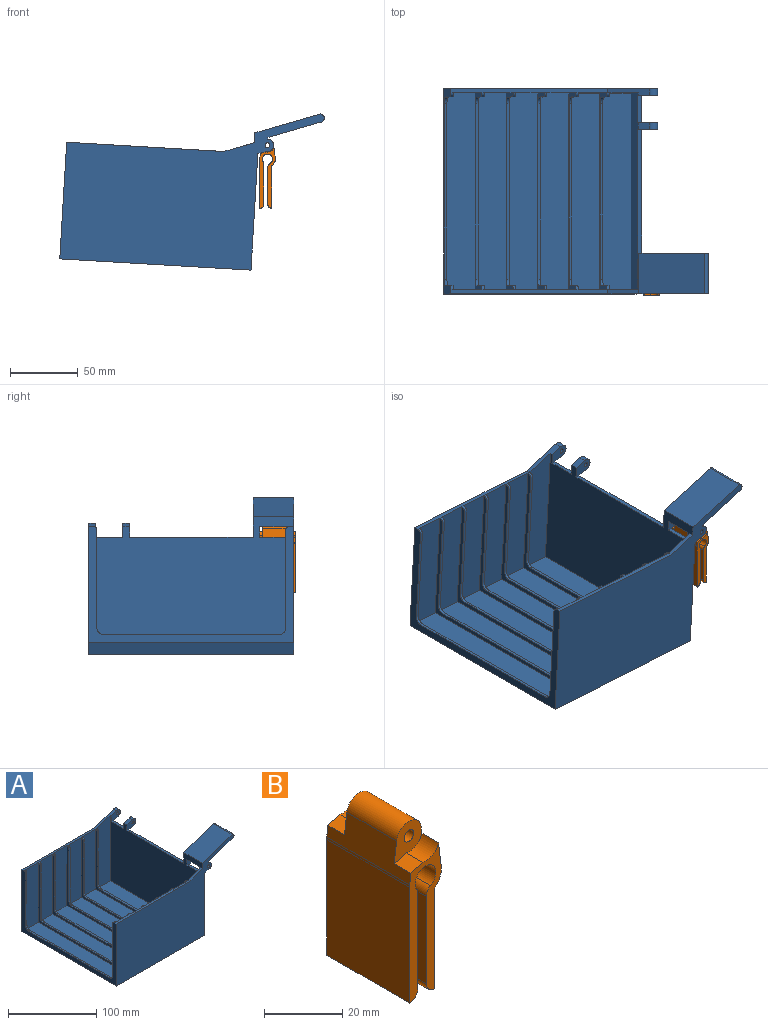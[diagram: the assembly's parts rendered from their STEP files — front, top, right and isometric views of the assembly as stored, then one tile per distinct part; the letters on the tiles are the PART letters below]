
ASSEMBLY  parts=2 mates=1
PART A: 109 faces, bbox 188.2x151x117.8 mm
  f0: cylinder r=4.5mm len=8.84mm, axis (0,1,0), area 64.7mm2, adj f89,f91,f92,f104
  f1: cylinder r=5mm len=20mm, axis (0,-1,0), area 79.2mm2, adj f88,f91,f104,f108
  f2: cylinder r=4.5mm len=8.84mm, axis (0,-1,0), area 64.7mm2, adj f8,f85,f88,f104
  f3: plane 91x3mm, normal (0,0,1), area 273mm2, adj f9,f26,f92,f103
  f4: plane 116x3mm, normal (0,0,1), area 348mm2, adj f10,f11,f14,f16,f19,f22,f29,f49
  f5: plane 20x3mm, normal (0,0,1), area 60mm2, adj f9,f26,f97,f102
  f6: plane 20x3mm, normal (0,0,1), area 60mm2, adj f9,f26,f88,f91
  f7: plane 145x83mm, normal (1,0,0), area 921.9mm2, adj f25,f27,f40,f43,f44,f45,f46,f47
  f8: plane 188.25x117.81mm, normal (0,-1,0), area 12641.2mm2, adj f2,f9,f11,f12,f26,f36,f85,f86
  f9: plane 151x86mm, normal (1,0,0), area 12986mm2, adj f3,f5,f6,f8,f10,f12,f85,f89
  f10: plane 152.25x97mm, normal (0,1,0), area 12320.9mm2, adj f4,f9,f11,f12,f93,f94,f95,f96
  f11: plane 151x86mm, normal (-1,0,0), area 1872.9mm2, adj f4,f8,f10,f12,f36,f71,f72,f73
  f12: plane 151x141mm, normal (0,0,-1), area 21291mm2, adj f8,f9,f10,f11
  f13: plane 145x83mm, normal (1,0,0), area 921.9mm2, adj f14,f35,f42,f78,f79,f80,f81,f82
  f14: plane 83x21mm, normal (0,-1,0), area 1743mm2, adj f4,f13,f15,f42
  f15: plane 145x83mm, normal (-1,0,0), area 921.9mm2, adj f14,f35,f42,f43,f44,f45,f46,f47
  f16: plane 83x21mm, normal (0,-1,0), area 1743mm2, adj f4,f17,f31,f37
  f17: plane 145x83mm, normal (-1,0,0), area 921.9mm2, adj f16,f18,f37,f78,f79,f80,f81,f82
  f18: plane 83x21mm, normal (0,1,0), area 1743mm2, adj f17,f31,f36,f37
  f19: plane 83x21mm, normal (0,-1,0), area 1743mm2, adj f4,f20,f32,f38
  f20: plane 145x83mm, normal (-1,0,0), area 921.9mm2, adj f19,f21,f38,f64,f65,f66,f67,f68
  f21: plane 83x21mm, normal (0,1,0), area 1743mm2, adj f20,f32,f36,f38
  f22: plane 83x21mm, normal (0,-1,0), area 1743mm2, adj f4,f23,f33,f39
  f23: plane 145x83mm, normal (-1,0,0), area 921.9mm2, adj f22,f24,f39,f57,f58,f59,f60,f61
  f24: plane 83x21mm, normal (0,1,0), area 1743mm2, adj f23,f33,f36,f39
  f25: plane 90.81x22mm, normal (0,-1,0), area 1828.9mm2, adj f7,f26,f40,f49,f96
  f26: plane 148x98.07mm, normal (-1,0,0), area 12362.2mm2, adj f3,f5,f6,f8,f25,f27,f40,f87
  f27: plane 90.81x22mm, normal (0,1,0), area 1828.9mm2, adj f7,f26,f40,f48,f87
  f28: plane 145x83mm, normal (1,0,0), area 921.9mm2, adj f29,f34,f41,f71,f72,f73,f74,f75
  f29: plane 83x21mm, normal (0,-1,0), area 1743mm2, adj f4,f28,f30,f41
  f30: plane 145x83mm, normal (-1,0,0), area 921.9mm2, adj f29,f34,f41,f50,f51,f52,f53,f54
  f31: plane 145x83mm, normal (1,0,0), area 921.9mm2, adj f16,f18,f37,f64,f65,f66,f67,f68
  f32: plane 145x83mm, normal (1,0,0), area 921.9mm2, adj f19,f21,f38,f57,f58,f59,f60,f61
  f33: plane 145x83mm, normal (1,0,0), area 921.9mm2, adj f22,f24,f39,f50,f51,f52,f53,f54
  f34: plane 83x21mm, normal (0,1,0), area 1743mm2, adj f28,f30,f36,f41
  f35: plane 83x21mm, normal (0,1,0), area 1743mm2, adj f13,f15,f36,f42
  f36: plane 116x3mm, normal (0,0,1), area 348mm2, adj f8,f11,f18,f21,f24,f34,f35,f48
  f37: plane 145x21mm, normal (0,0,1), area 3045mm2, adj f16,f17,f18,f31
  f38: plane 145x21mm, normal (0,0,1), area 3045mm2, adj f19,f20,f21,f32
  f39: plane 145x21mm, normal (0,0,1), area 3045mm2, adj f22,f23,f24,f33
  f40: plane 145x21mm, normal (0,0,1), area 3045mm2, adj f7,f25,f26,f27
  f41: plane 145x21mm, normal (0,0,1), area 3045mm2, adj f28,f29,f30,f34
  f42: plane 145x21mm, normal (0,0,1), area 3045mm2, adj f13,f14,f15,f35
  f43: plane 72x2mm, normal (0,1,0), area 144mm2, adj f7,f15,f44,f48
  f44: cylinder r=5mm len=5mm, axis (-1,0,0), area 15.7mm2, adj f7,f15,f43,f45
  f45: plane 129x2mm, normal (0,0,1), area 258mm2, adj f7,f15,f44,f46
  f46: cylinder r=5mm len=5mm, axis (-1,0,0), area 15.7mm2, adj f7,f15,f45,f47
  f47: plane 72x2mm, normal (0,-1,0), area 144mm2, adj f7,f15,f46,f49
  f48: cylinder r=3mm len=3mm, axis (-1,0,0), area 9.4mm2, adj f7,f15,f27,f36,f43
  f49: cylinder r=3mm len=3mm, axis (-1,0,0), area 9.4mm2, adj f4,f7,f15,f25,f47
  f50: cylinder r=3mm len=3mm, axis (-1,0,0), area 9.4mm2, adj f30,f33,f36,f51
  f51: plane 72x2mm, normal (0,1,0), area 144mm2, adj f30,f33,f50,f52
  f52: cylinder r=5mm len=5mm, axis (-1,0,0), area 15.7mm2, adj f30,f33,f51,f53
  f53: plane 129x2mm, normal (0,0,1), area 258mm2, adj f30,f33,f52,f54
  f54: cylinder r=5mm len=5mm, axis (-1,0,0), area 15.7mm2, adj f30,f33,f53,f55
  f55: plane 72x2mm, normal (0,-1,0), area 144mm2, adj f30,f33,f54,f56
  f56: cylinder r=3mm len=3mm, axis (-1,0,0), area 9.4mm2, adj f4,f30,f33,f55
  f57: cylinder r=3mm len=3mm, axis (-1,0,0), area 9.4mm2, adj f23,f32,f36,f58
  f58: plane 72x2mm, normal (0,1,0), area 144mm2, adj f23,f32,f57,f59
  f59: cylinder r=5mm len=5mm, axis (-1,0,0), area 15.7mm2, adj f23,f32,f58,f60
  f60: plane 129x2mm, normal (0,0,1), area 258mm2, adj f23,f32,f59,f61
  f61: cylinder r=5mm len=5mm, axis (-1,0,0), area 15.7mm2, adj f23,f32,f60,f62
  f62: plane 72x2mm, normal (0,-1,0), area 144mm2, adj f23,f32,f61,f63
  f63: cylinder r=3mm len=3mm, axis (-1,0,0), area 9.4mm2, adj f4,f23,f32,f62
  f64: cylinder r=3mm len=3mm, axis (-1,0,0), area 9.4mm2, adj f20,f31,f36,f65
  f65: plane 72x2mm, normal (0,1,0), area 144mm2, adj f20,f31,f64,f66
  f66: cylinder r=5mm len=5mm, axis (-1,0,0), area 15.7mm2, adj f20,f31,f65,f67
  f67: plane 129x2mm, normal (0,0,1), area 258mm2, adj f20,f31,f66,f68
  f68: cylinder r=5mm len=5mm, axis (-1,0,0), area 15.7mm2, adj f20,f31,f67,f69
  f69: plane 72x2mm, normal (0,-1,0), area 144mm2, adj f20,f31,f68,f70
  f70: cylinder r=3mm len=3mm, axis (-1,0,0), area 9.4mm2, adj f4,f20,f31,f69
  f71: cylinder r=3mm len=3mm, axis (-1,0,0), area 9.4mm2, adj f11,f28,f36,f72
  f72: plane 72x2mm, normal (0,1,0), area 144mm2, adj f11,f28,f71,f73
  f73: cylinder r=5mm len=5mm, axis (-1,0,0), area 15.7mm2, adj f11,f28,f72,f74
  f74: plane 129x2mm, normal (0,0,1), area 258mm2, adj f11,f28,f73,f75
  f75: cylinder r=5mm len=5mm, axis (-1,0,0), area 15.7mm2, adj f11,f28,f74,f76
  f76: plane 72x2mm, normal (0,-1,0), area 144mm2, adj f11,f28,f75,f77
  f77: cylinder r=3mm len=3mm, axis (-1,0,0), area 9.4mm2, adj f4,f11,f28,f76
  f78: plane 72x2mm, normal (0,-1,0), area 144mm2, adj f13,f17,f79,f83
  f79: cylinder r=5mm len=5mm, axis (-1,0,0), area 15.7mm2, adj f13,f17,f78,f80
  f80: plane 129x2mm, normal (0,0,1), area 258mm2, adj f13,f17,f79,f81
  f81: cylinder r=5mm len=5mm, axis (-1,0,0), area 15.7mm2, adj f13,f17,f80,f82
  f82: plane 72x2mm, normal (0,1,0), area 144mm2, adj f13,f17,f81,f84
  f83: cylinder r=3mm len=3mm, axis (-1,0,0), area 9.4mm2, adj f4,f13,f17,f78
  f84: cylinder r=3mm len=3mm, axis (-1,0,0), area 9.4mm2, adj f13,f17,f36,f82
  f85: plane 7.93x5mm, normal (0.26,0,-0.96), area 41.1mm2, adj f2,f8,f9,f88
  f86: cylinder r=1.75mm len=5mm, axis (0,-1,0), area 55mm2, adj f8,f88
  f87: plane 22x7.81mm, normal (-0.33,0,0.94), area 70mm2, adj f8,f26,f27,f36
  f88: plane 14.25x11.5mm, normal (0,1,0), area 110.5mm2, adj f1,f2,f6,f26,f85,f86,f104,f108
  f89: plane 7.93x5mm, normal (0.26,0,-0.96), area 41.1mm2, adj f0,f9,f91,f92
  f90: cylinder r=1.75mm len=5mm, axis (0,1,0), area 55mm2, adj f91,f92
  f91: plane 14.25x11.5mm, normal (0,-1,0), area 110.5mm2, adj f0,f1,f6,f26,f89,f90,f104,f108
  f92: plane 50.25x31.81mm, normal (0,1,0), area 429.2mm2, adj f0,f3,f26,f89,f90,f104,f105,f106
  f93: plane 7.93x5mm, normal (0.26,0,-0.96), area 41.1mm2, adj f9,f10,f94,f97
  f94: cylinder r=4.5mm len=8.84mm, axis (0,1,0), area 72.4mm2, adj f10,f93,f96,f97
  f95: cylinder r=1.75mm len=5mm, axis (0,1,0), area 55mm2, adj f10,f97
  f96: plane 30.24x10.74mm, normal (-0.33,0,0.94), area 113.8mm2, adj f4,f10,f25,f26,f94,f97
  f97: plane 14.25x11mm, normal (0,-1,0), area 109mm2, adj f5,f26,f93,f94,f95,f96
  f98: cylinder r=4.5mm len=8.84mm, axis (0,-1,0), area 72.4mm2, adj f99,f100,f102,f103
  f99: plane 7.93x5mm, normal (0.26,0,-0.96), area 41.1mm2, adj f9,f98,f102,f103
  f100: plane 8.24x5mm, normal (-0.33,0,0.94), area 43.7mm2, adj f26,f98,f102,f103
  f101: cylinder r=1.75mm len=5mm, axis (0,-1,0), area 55mm2, adj f102,f103
  f102: plane 14.25x11mm, normal (0,1,0), area 109mm2, adj f5,f26,f98,f99,f100,f101
  f103: plane 14.25x11mm, normal (0,-1,0), area 109mm2, adj f3,f26,f98,f99,f100,f101
  f104: plane 30x1.28mm, normal (1,0,0), area 28.3mm2, adj f0,f1,f2,f8,f88,f91,f92,f105
  f105: plane 37.37x30mm, normal (0.33,0,-0.94), area 1189.6mm2, adj f8,f92,f104,f106
  f106: cylinder r=3.13mm len=30mm, axis (0,-1,0), area 295mm2, adj f8,f92,f105,f107
  f107: plane 47.12x30mm, normal (-0.33,0,0.94), area 1500mm2, adj f8,f26,f92,f106
  f108: plane 20x6.19mm, normal (0.33,0,-0.94), area 131.4mm2, adj f1,f26,f88,f91
PART B: 22 faces, bbox 11.5x30x51 mm
  f0: plane 30x10.1mm, normal (0.99,0,0.12), area 279.1mm2, adj f1,f5,f11,f12,f13,f14,f16,f18
  f1: cylinder r=4.5mm len=18mm, axis (0,-1,0), area 234.7mm2, adj f0,f6,f13,f18
  f2: cylinder r=1.75mm len=18mm, axis (0,-1,0), area 197.9mm2, adj f13,f18
  f3: plane 30x27.33mm, normal (-1,0,0), area 820mm2, adj f11,f12,f19,f20
  f4: plane 31.51x30mm, normal (1,0,0), area 945.2mm2, adj f5,f11,f12,f19
  f5: cylinder r=5.75mm len=30mm, axis (0,-1,0), area 188.4mm2, adj f0,f4,f11,f12
  f6: plane 30x10.1mm, normal (-0.99,0,0.12), area 224.8mm2, adj f1,f7,f11,f12,f13,f15,f17,f18
  f7: cylinder r=5.75mm len=30mm, axis (0,-1,0), area 21.1mm2, adj f6,f8,f11,f12
  f8: plane 36.25x30mm, normal (-1,0,0), area 1087.5mm2, adj f7,f11,f12,f21
  f9: plane 30.7x30mm, normal (1,0,0), area 921mm2, adj f10,f11,f12,f21
  f10: cylinder r=3.75mm len=30mm, axis (0,-1,0), area 557.7mm2, adj f9,f11,f12,f20
  f11: plane 44.89x11.5mm, normal (0,1,0), area 247.6mm2, adj f0,f3,f4,f5,f6,f7,f8,f9
  f12: plane 44.89x11.5mm, normal (0,-1,0), area 247.6mm2, adj f0,f3,f4,f5,f6,f7,f8,f9
  f13: plane 10.6x10.02mm, normal (0,-1,0), area 67.7mm2, adj f0,f1,f2,f6,f14,f15
  f14: cylinder r=5mm len=6mm, axis (0,-1,0), area 42.8mm2, adj f0,f12,f13,f15
  f15: plane 6x4.36mm, normal (-0.26,0,0.96), area 27.1mm2, adj f6,f12,f13,f14
  f16: cylinder r=5mm len=6mm, axis (0,1,0), area 42.8mm2, adj f0,f11,f17,f18
  f17: plane 6x4.36mm, normal (-0.26,0,0.96), area 27.1mm2, adj f6,f11,f16,f18
  f18: plane 10.6x10.02mm, normal (0,1,0), area 67.7mm2, adj f0,f1,f2,f6,f16,f17
  f19: cylinder r=3mm len=30mm, axis (0,1,0), area 141.4mm2, adj f3,f4,f11,f12
  f20: cylinder r=3mm len=30mm, axis (0,-1,0), area 96.2mm2, adj f3,f10,f11,f12
  f21: cylinder r=3mm len=30mm, axis (0,1,0), area 141.4mm2, adj f8,f9,f11,f12
PLACE A rot(axis=(0,1,0),3.4deg) t=(-5.25,0.5,0.73)mm
PLACE B t=(0,-0.5,0)mm fixed
MATE revolute A.f1 <-> B.f1  axis (0,-1,0) through (9.75,-70,89.5)mm
